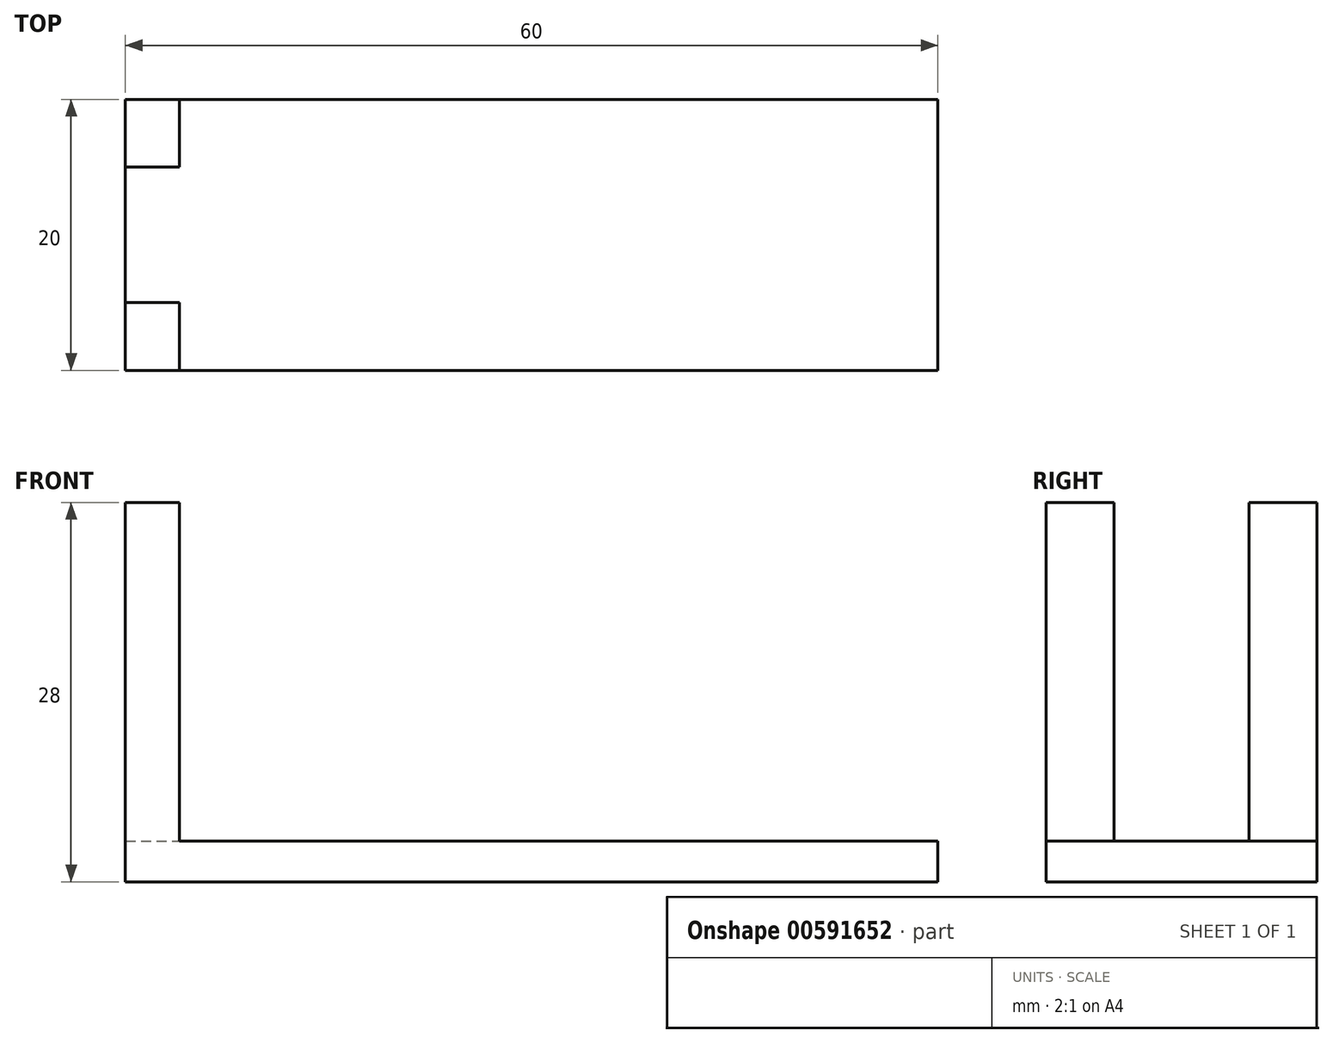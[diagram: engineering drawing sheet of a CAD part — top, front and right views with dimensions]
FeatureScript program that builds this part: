
annotation { "Feature Type Name" : "Feature", "Feature Type Description" : "" }
export const myFeature = defineFeature(function(context is Context, id is Id, definition is map)
    precondition{}
    {
        {
            var Q0;
            Q0=qCreatedBy(makeId("Top.planeOp"),FACE);
            var sketch = newSketch(context, id + "F0", { "sketchPlane" : qUnion([Q0])});
            skLineSegment(sketch, "E0.bottom", {"start": v(30, -10) * mm, "end": v(-30, -10) * mm});
            skLineSegment(sketch, "E0.top", {"start": v(30, 10) * mm, "end": v(-30, 10) * mm});
            skLineSegment(sketch, "E0.left", {"start": v(30, -10) * mm, "end": v(30, 10) * mm});
            skLineSegment(sketch, "E0.right", {"start": v(-30, -10) * mm, "end": v(-30, 10) * mm});
            skPoint(sketch, "E0.middle", {"position": v(0, 0) * mm});
            skSolve(sketch);
        }
        {
            var Q0;
            Q0 = qSketchRegion(id + "F0", true);
            extrude(context, id + "F1", {"entities" : qUnion([Q0]), "depth" : 3 * mm, "offsetDistance" : 25 * mm});
        }
        {
            var Q0;
            Q0=makeQuery(id+"F1.opExtrude","CAP_FACE",FACE,{"disambiguationData":[OSD([sQuery(id+"F0.wireOp",EDGE,"E0.bottom"),sQuery(id+"F0.wireOp",EDGE,"E0.top"),sQuery(id+"F0.wireOp",EDGE,"E0.left"),sQuery(id+"F0.wireOp",EDGE,"E0.right")])],"isStart":false});
            var sketch = newSketch(context, id + "F2", { "sketchPlane" : qUnion([Q0])});
            skLineSegment(sketch, "E1.bottom", {"start": v(-30, 10) * mm, "end": v(-26, 10) * mm});
            skLineSegment(sketch, "E1.top", {"start": v(-30, -10) * mm, "end": v(-26, -10) * mm});
            skLineSegment(sketch, "E1.left", {"start": v(-30, 10) * mm, "end": v(-30, -10) * mm});
            skLineSegment(sketch, "E1.right", {"start": v(-26, 10) * mm, "end": v(-26, -10) * mm});
            skSolve(sketch);
        }
        {
            var Q0;
            Q0 = qSketchRegion(id + "F2", true);
            extrude(context, id + "F3", {"entities" : qUnion([Q0]), "operationType" : NewBodyOperationType.ADD, "depth" : 25 * mm, "offsetDistance" : 25 * mm});
        }
        {
            var Q0;
            Q0=qCreatedBy(makeId("Front.planeOp"),FACE);
            var sketch = newSketch(context, id + "F4", { "sketchPlane" : qUnion([Q0])});
            skLineSegment(sketch, "E2.bottom", {"start": v(-30, 28) * mm, "end": v(30, 28) * mm});
            skLineSegment(sketch, "E2.top", {"start": v(-30, 3) * mm, "end": v(30, 3) * mm});
            skLineSegment(sketch, "E2.left", {"start": v(-30, 28) * mm, "end": v(-30, 3) * mm});
            skLineSegment(sketch, "E2.right", {"start": v(30, 28) * mm, "end": v(30, 3) * mm});
            skSolve(sketch);
        }
        {
            var Q0;
            Q0 = qSketchRegion(id + "F4", true);
            extrude(context, id + "F5", {"entities" : qUnion([Q0]), "operationType" : NewBodyOperationType.REMOVE, "endBound" : BoundingType.SYMMETRIC, "oppositeDirection" : true, "depth" : 10 * mm, "offsetDistance" : 25 * mm});
        }
    });
